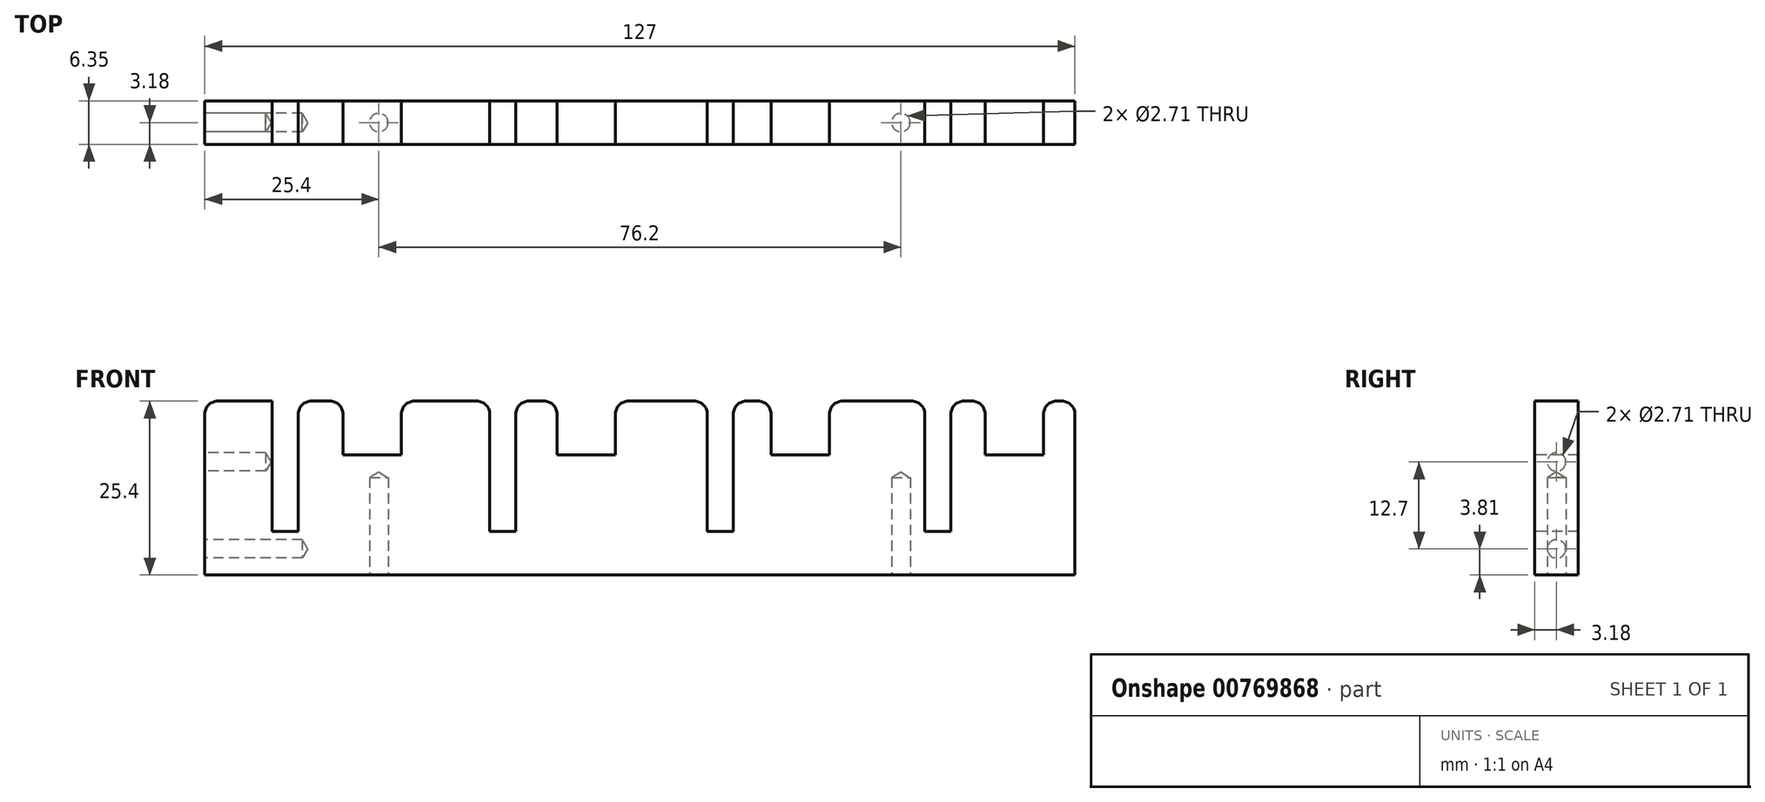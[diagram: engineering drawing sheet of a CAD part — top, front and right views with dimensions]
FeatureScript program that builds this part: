
annotation { "Feature Type Name" : "Feature", "Feature Type Description" : "" }
export const myFeature = defineFeature(function(context is Context, id is Id, definition is map)
    precondition{}
    {
        {
            var Q0;
            Q0=qCreatedBy(makeId("Top.planeOp"),FACE);
            var sketch = newSketch(context, id + "F0", { "sketchPlane" : qUnion([Q0])});
            skLineSegment(sketch, "E0.bottom", {"start": v(-63.5, 3.18) * mm, "end": v(63.5, 3.18) * mm});
            skLineSegment(sketch, "E0.top", {"start": v(-63.5, -3.17) * mm, "end": v(63.5, -3.17) * mm});
            skLineSegment(sketch, "E0.left", {"start": v(-63.5, 3.18) * mm, "end": v(-63.5, -3.17) * mm});
            skLineSegment(sketch, "E0.right", {"start": v(63.5, 3.18) * mm, "end": v(63.5, -3.17) * mm});
            skLineSegment(sketch, "E1", {"start": v(-63.5, 3.18) * mm, "end": v(63.5, -3.17) * mm, "construction": true});
            skPoint(sketch, "E2", {"position": v(0, 0) * mm});
            skSolve(sketch);
        }
        {
            var Q0;
            Q0=qSketchRegion(id+"F0",true);
            extrude(context, id + "F1", {"entities" : qUnion([Q0]), "depth" : 25.4 * mm, "offsetDistance" : 25.4 * mm});
        }
        {
            var Q0;
            Q0=makeQuery(id+"F1.opExtrude","SWEPT_FACE",FACE,{"disambiguationData":[OSD([sQuery(id+"F0.wireOp",EDGE,"E0.top")])]});
            var sketch = newSketch(context, id + "F2", { "sketchPlane" : qUnion([Q0])});
            skLineSegment(sketch, "E3", {"start": v(-53.66, 25.4) * mm, "end": v(-53.66, 6.35) * mm});
            skLineSegment(sketch, "E4", {"start": v(-53.66, 6.35) * mm, "end": v(-49.85, 6.35) * mm});
            skLineSegment(sketch, "E5", {"start": v(-49.85, 6.35) * mm, "end": v(-49.85, 25.4) * mm});
            skLineSegment(sketch, "E6", {"start": v(-53.66, 25.4) * mm, "end": v(-49.85, 25.4) * mm});
            skLineSegment(sketch, "E7.1.0.0", {"start": v(-21.9, 25.4) * mm, "end": v(-18.1, 25.4) * mm});
            skLineSegment(sketch, "E7.1.0.1", {"start": v(-21.9, 25.4) * mm, "end": v(-21.9, 6.35) * mm});
            skLineSegment(sketch, "E7.1.0.2", {"start": v(-18.1, 6.35) * mm, "end": v(-18.1, 25.4) * mm});
            skLineSegment(sketch, "E7.1.0.3", {"start": v(-21.9, 6.35) * mm, "end": v(-18.1, 6.35) * mm});
            skLineSegment(sketch, "E7.2.0.0", {"start": v(9.84, 25.4) * mm, "end": v(13.65, 25.4) * mm});
            skLineSegment(sketch, "E7.2.0.1", {"start": v(9.84, 25.4) * mm, "end": v(9.84, 6.35) * mm});
            skLineSegment(sketch, "E7.2.0.2", {"start": v(13.65, 6.35) * mm, "end": v(13.65, 25.4) * mm});
            skLineSegment(sketch, "E7.2.0.3", {"start": v(9.84, 6.35) * mm, "end": v(13.65, 6.35) * mm});
            skLineSegment(sketch, "E7.3.0.0", {"start": v(41.6, 25.4) * mm, "end": v(45.4, 25.4) * mm});
            skLineSegment(sketch, "E7.3.0.1", {"start": v(41.6, 25.4) * mm, "end": v(41.6, 6.35) * mm});
            skLineSegment(sketch, "E7.3.0.2", {"start": v(45.4, 6.35) * mm, "end": v(45.4, 25.4) * mm});
            skLineSegment(sketch, "E7.3.0.3", {"start": v(41.6, 6.35) * mm, "end": v(45.4, 6.35) * mm});
            skLineSegment(sketch, "E7.direction1", {"start": v(-53.66, 6.35) * mm, "end": v(-21.9, 6.35) * mm, "construction": true});
            skPoint(sketch, "E8", {"position": v(-51.75, 6.35) * mm});
            skLineSegment(sketch, "E9.bottom", {"start": v(-43.33, 25.4) * mm, "end": v(-34.8, 25.4) * mm});
            skLineSegment(sketch, "E9.top", {"start": v(-43.33, 17.53) * mm, "end": v(-34.8, 17.53) * mm});
            skLineSegment(sketch, "E9.left", {"start": v(-43.33, 25.4) * mm, "end": v(-43.33, 17.53) * mm});
            skLineSegment(sketch, "E9.right", {"start": v(-34.8, 25.4) * mm, "end": v(-34.8, 17.53) * mm});
            skLineSegment(sketch, "E10.1.0.0", {"start": v(-3.56, 25.4) * mm, "end": v(-3.56, 17.53) * mm});
            skLineSegment(sketch, "E10.1.0.1", {"start": v(-12.1, 17.53) * mm, "end": v(-3.56, 17.53) * mm});
            skLineSegment(sketch, "E10.1.0.2", {"start": v(-12.1, 25.4) * mm, "end": v(-3.56, 25.4) * mm});
            skLineSegment(sketch, "E10.1.0.3", {"start": v(-12.1, 25.4) * mm, "end": v(-12.1, 17.53) * mm});
            skLineSegment(sketch, "E10.2.0.0", {"start": v(27.69, 25.4) * mm, "end": v(27.69, 17.53) * mm});
            skLineSegment(sketch, "E10.2.0.1", {"start": v(19.15, 17.53) * mm, "end": v(27.69, 17.53) * mm});
            skLineSegment(sketch, "E10.2.0.2", {"start": v(19.15, 25.4) * mm, "end": v(27.69, 25.4) * mm});
            skLineSegment(sketch, "E10.2.0.3", {"start": v(19.15, 25.4) * mm, "end": v(19.15, 17.53) * mm});
            skLineSegment(sketch, "E10.3.0.0", {"start": v(58.93, 25.4) * mm, "end": v(58.93, 17.53) * mm});
            skLineSegment(sketch, "E10.3.0.1", {"start": v(50.4, 17.53) * mm, "end": v(58.93, 17.53) * mm});
            skLineSegment(sketch, "E10.3.0.2", {"start": v(50.4, 25.4) * mm, "end": v(58.93, 25.4) * mm});
            skLineSegment(sketch, "E10.3.0.3", {"start": v(50.4, 25.4) * mm, "end": v(50.4, 17.53) * mm});
            skLineSegment(sketch, "E10.direction1", {"start": v(-43.33, 17.53) * mm, "end": v(-12.1, 17.53) * mm, "construction": true});
            skPoint(sketch, "E11", {"position": v(-34.8, 21.46) * mm});
            skPoint(sketch, "E12", {"position": v(-39.07, 25.4) * mm});
            skSolve(sketch);
        }
        {
            var Q0;
            Q0=qSketchRegion(id+"F2",true);
            extrude(context, id + "F3", {"entities" : qUnion([Q0]), "operationType" : NewBodyOperationType.REMOVE, "endBound" : BoundingType.UP_TO_NEXT, "oppositeDirection" : true, "depth" : 25.4 * mm, "offsetDistance" : 25.4 * mm});
        }
        {
            var Q0;
            Q0=makeQuery(id+"F3.boolean.opBoolean","COPY",EDGE,{"derivedFrom":makeQuery(id+"F3.opExtrude","SWEPT_EDGE",EDGE,{"disambiguationData":[OSD([sQuery(id+"F0.wireOp",EDGE,"E0.top"),sQuery(id+"F2.wireOp",EDGE,"E3"),sQuery(id+"F2.wireOp",EDGE,"E6")])]})});
            var Q1;
            Q1=makeQuery(id+"F3.boolean.opBoolean","COPY",EDGE,{"derivedFrom":makeQuery(id+"F3.opExtrude","SWEPT_EDGE",EDGE,{"disambiguationData":[OSD([sQuery(id+"F0.wireOp",EDGE,"E0.top"),sQuery(id+"F2.wireOp",EDGE,"E5"),sQuery(id+"F2.wireOp",EDGE,"E6")])]})});
            var Q2;
            Q2=makeQuery(id+"F3.boolean.opBoolean","COPY",EDGE,{"derivedFrom":makeQuery(id+"F3.opExtrude","SWEPT_EDGE",EDGE,{"disambiguationData":[OSD([sQuery(id+"F0.wireOp",EDGE,"E0.top"),sQuery(id+"F2.wireOp",EDGE,"E7.1.0.0"),sQuery(id+"F2.wireOp",EDGE,"E7.1.0.1")])]})});
            var Q3;
            Q3=makeQuery(id+"F3.boolean.opBoolean","COPY",EDGE,{"derivedFrom":makeQuery(id+"F3.opExtrude","SWEPT_EDGE",EDGE,{"disambiguationData":[OSD([sQuery(id+"F0.wireOp",EDGE,"E0.top"),sQuery(id+"F2.wireOp",EDGE,"E7.1.0.0"),sQuery(id+"F2.wireOp",EDGE,"E7.1.0.2")])]})});
            var Q4;
            Q4=makeQuery(id+"F3.boolean.opBoolean","COPY",EDGE,{"derivedFrom":makeQuery(id+"F3.opExtrude","SWEPT_EDGE",EDGE,{"disambiguationData":[OSD([sQuery(id+"F0.wireOp",EDGE,"E0.top"),sQuery(id+"F2.wireOp",EDGE,"E7.2.0.0"),sQuery(id+"F2.wireOp",EDGE,"E7.2.0.1")])]})});
            var Q5;
            Q5=makeQuery(id+"F3.boolean.opBoolean","COPY",EDGE,{"derivedFrom":makeQuery(id+"F3.opExtrude","SWEPT_EDGE",EDGE,{"disambiguationData":[OSD([sQuery(id+"F0.wireOp",EDGE,"E0.top"),sQuery(id+"F2.wireOp",EDGE,"E7.2.0.0"),sQuery(id+"F2.wireOp",EDGE,"E7.2.0.2")])]})});
            var Q6;
            Q6=makeQuery(id+"F3.boolean.opBoolean","COPY",EDGE,{"derivedFrom":makeQuery(id+"F3.opExtrude","SWEPT_EDGE",EDGE,{"disambiguationData":[OSD([sQuery(id+"F0.wireOp",EDGE,"E0.top"),sQuery(id+"F2.wireOp",EDGE,"E7.3.0.0"),sQuery(id+"F2.wireOp",EDGE,"E7.3.0.1")])]})});
            var Q7;
            Q7=makeQuery(id+"F3.boolean.opBoolean","COPY",EDGE,{"derivedFrom":makeQuery(id+"F3.opExtrude","SWEPT_EDGE",EDGE,{"disambiguationData":[OSD([sQuery(id+"F0.wireOp",EDGE,"E0.top"),sQuery(id+"F2.wireOp",EDGE,"E7.3.0.0"),sQuery(id+"F2.wireOp",EDGE,"E7.3.0.2")])]})});
            var Q8;
            Q8=makeQuery(id+"F3.boolean.opBoolean","COPY",EDGE,{"derivedFrom":makeQuery(id+"F3.opExtrude","SWEPT_EDGE",EDGE,{"disambiguationData":[OSD([sQuery(id+"F0.wireOp",EDGE,"E0.top"),sQuery(id+"F2.wireOp",EDGE,"E9.bottom"),sQuery(id+"F2.wireOp",EDGE,"E9.left")])]})});
            var Q9;
            Q9=makeQuery(id+"F3.boolean.opBoolean","COPY",EDGE,{"derivedFrom":makeQuery(id+"F3.opExtrude","SWEPT_EDGE",EDGE,{"disambiguationData":[OSD([sQuery(id+"F0.wireOp",EDGE,"E0.top"),sQuery(id+"F2.wireOp",EDGE,"E9.bottom"),sQuery(id+"F2.wireOp",EDGE,"E9.right")])]})});
            var Q10;
            Q10=makeQuery(id+"F3.boolean.opBoolean","COPY",EDGE,{"derivedFrom":makeQuery(id+"F3.opExtrude","SWEPT_EDGE",EDGE,{"disambiguationData":[OSD([sQuery(id+"F0.wireOp",EDGE,"E0.top"),sQuery(id+"F2.wireOp",EDGE,"E10.1.0.2"),sQuery(id+"F2.wireOp",EDGE,"E10.1.0.3")])]})});
            var Q11;
            Q11=makeQuery(id+"F3.boolean.opBoolean","COPY",EDGE,{"derivedFrom":makeQuery(id+"F3.opExtrude","SWEPT_EDGE",EDGE,{"disambiguationData":[OSD([sQuery(id+"F0.wireOp",EDGE,"E0.top"),sQuery(id+"F2.wireOp",EDGE,"E10.1.0.0"),sQuery(id+"F2.wireOp",EDGE,"E10.1.0.2")])]})});
            var Q12;
            Q12=makeQuery(id+"F3.boolean.opBoolean","COPY",EDGE,{"derivedFrom":makeQuery(id+"F3.opExtrude","SWEPT_EDGE",EDGE,{"disambiguationData":[OSD([sQuery(id+"F0.wireOp",EDGE,"E0.top"),sQuery(id+"F2.wireOp",EDGE,"E10.2.0.2"),sQuery(id+"F2.wireOp",EDGE,"E10.2.0.3")])]})});
            var Q13;
            Q13=makeQuery(id+"F3.boolean.opBoolean","COPY",EDGE,{"derivedFrom":makeQuery(id+"F3.opExtrude","SWEPT_EDGE",EDGE,{"disambiguationData":[OSD([sQuery(id+"F0.wireOp",EDGE,"E0.top"),sQuery(id+"F2.wireOp",EDGE,"E10.2.0.0"),sQuery(id+"F2.wireOp",EDGE,"E10.2.0.2")])]})});
            var Q14;
            Q14=makeQuery(id+"F3.boolean.opBoolean","COPY",EDGE,{"derivedFrom":makeQuery(id+"F3.opExtrude","SWEPT_EDGE",EDGE,{"disambiguationData":[OSD([sQuery(id+"F0.wireOp",EDGE,"E0.top"),sQuery(id+"F2.wireOp",EDGE,"E10.3.0.2"),sQuery(id+"F2.wireOp",EDGE,"E10.3.0.3")])]})});
            var Q15;
            Q15=makeQuery(id+"F3.boolean.opBoolean","COPY",EDGE,{"derivedFrom":makeQuery(id+"F3.opExtrude","SWEPT_EDGE",EDGE,{"disambiguationData":[OSD([sQuery(id+"F0.wireOp",EDGE,"E0.top"),sQuery(id+"F2.wireOp",EDGE,"E10.3.0.0"),sQuery(id+"F2.wireOp",EDGE,"E10.3.0.2")])]})});
            var Q16;
            Q16=makeQuery(id+"F1.opExtrude","CAP_EDGE",EDGE,{"disambiguationData":[OSD([sQuery(id+"F0.wireOp",EDGE,"E0.right")])],"isStart":false});
            var Q17;
            Q17=makeQuery(id+"F1.opExtrude","CAP_EDGE",EDGE,{"disambiguationData":[OSD([sQuery(id+"F0.wireOp",EDGE,"E0.left")])],"isStart":false});
            fillet(context, id + "F4", {"entities" : qUnion([Q0, Q1, Q2, Q3, Q4, Q5, Q6, Q7, Q8, Q9, Q10, Q11, Q12, Q13, Q14, Q15, Q16, Q17]), "radius" : 1.9 * mm, "tangentPropagation" : true, "allowEdgeOverflow" : false});
        }
        {
            var Q0;
            Q0=makeQuery(id+"F1.opExtrude","CAP_FACE",FACE,{"disambiguationData":[OSD([sQuery(id+"F0.wireOp",EDGE,"E0.bottom"),sQuery(id+"F0.wireOp",EDGE,"E0.top"),sQuery(id+"F0.wireOp",EDGE,"E0.left"),sQuery(id+"F0.wireOp",EDGE,"E0.right")])],"isStart":true});
            var sketch = newSketch(context, id + "F5", { "sketchPlane" : qUnion([Q0])});
            skLineSegment(sketch, "E13", {"start": v(-63.5, 0) * mm, "end": v(63.5, 0) * mm, "construction": true});
            skPoint(sketch, "E14", {"position": v(-38.1, 0) * mm});
            skPoint(sketch, "E15", {"position": v(38.1, 0) * mm});
            skSolve(sketch);
        }
        {
            var Q0;
            Q0=makeQuery(id+"F1.opExtrude","SWEPT_FACE",FACE,{"disambiguationData":[OSD([sQuery(id+"F0.wireOp",EDGE,"E0.left")])]});
            var sketch = newSketch(context, id + "F6", { "sketchPlane" : qUnion([Q0])});
            skLineSegment(sketch, "E16", {"start": v(0, 23.5) * mm, "end": v(0, 0) * mm, "construction": true});
            skPoint(sketch, "E17", {"position": v(0, 3.81) * mm});
            skPoint(sketch, "E18", {"position": v(0, 16.51) * mm});
            skSolve(sketch);
        }
        {
            var Q0;
            Q0=sQuery(id+"F5.wireOp",VERTEX,"E14");
            var Q1;
            Q1=sQuery(id+"F5.wireOp",VERTEX,"E15");
            var Q2;
            Q2=sQuery(id+"F6.wireOp",VERTEX,"E17");
            var Q3;
            Q3=makeQuery(id+"F1.opExtrude","SWEPT_BODY",BODY,{"disambiguationData":[OSD([sQuery(id+"F0.wireOp",EDGE,"E0.bottom"),sQuery(id+"F0.wireOp",EDGE,"E0.top"),sQuery(id+"F0.wireOp",EDGE,"E0.left"),sQuery(id+"F0.wireOp",EDGE,"E0.right")])]});
            hole(context, id + "F7", {"style" : HoleStyle.SIMPLE, "endStyle" : HoleEndStyle.BLIND, "standardTappedOrClearance" : lookupTablePath({ "standard" : "ANSI", "engagement" : "75%", "pitch" : "32 tpi", "size" : "#6", "type" : "Tapped" }), "standardBlindInLast" : lookupTablePath({ "standard" : "ANSI", "engagement" : "75%", "pitch" : "32 tpi", "size" : "#6", "type" : "Tapped" }), "holeDiameter" : 2.7 * mm, "majorDiameter" : 3.5 * mm, "showTappedDepth" : true, "holeDepth" : 14.22 * mm, "tappedDepth" : 11.84 * mm, "tapClearance" : 3, "locations" : qUnion([Q0, Q1, Q2]), "scope" : qUnion([Q3])});
        }
        {
            var Q0;
            Q0=sQuery(id+"F6.wireOp",VERTEX,"E18");
            var Q1;
            Q1=makeQuery(id+"F1.opExtrude","SWEPT_BODY",BODY,{"disambiguationData":[OSD([sQuery(id+"F0.wireOp",EDGE,"E0.bottom"),sQuery(id+"F0.wireOp",EDGE,"E0.top"),sQuery(id+"F0.wireOp",EDGE,"E0.left"),sQuery(id+"F0.wireOp",EDGE,"E0.right")])]});
            hole(context, id + "F8", {"style" : HoleStyle.SIMPLE, "endStyle" : HoleEndStyle.BLIND, "standardTappedOrClearance" : lookupTablePath({ "standard" : "ANSI", "engagement" : "75%", "pitch" : "32 tpi", "size" : "#6", "type" : "Tapped" }), "standardBlindInLast" : lookupTablePath({ "fit" : "Free", "standard" : "ANSI", "engagement" : "75%", "pitch" : "32 tpi", "size" : "#6", "type" : "Clearance & tapped" }), "holeDiameter" : 2.7 * mm, "majorDiameter" : 3.5 * mm, "showTappedDepth" : true, "holeDepth" : 8.9 * mm, "tappedDepth" : 6.5 * mm, "tapClearance" : 3, "locations" : qUnion([Q0]), "scope" : qUnion([Q1])});
        }
    });
